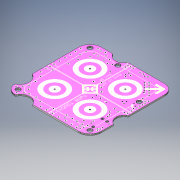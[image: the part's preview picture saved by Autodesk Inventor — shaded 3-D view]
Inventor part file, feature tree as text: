
AUTODESK INVENTOR PART (.ipt)
format: ipt  version: 2016 (Build 200138000, 138)  size: 2,645,504 bytes
history: native  units: in
note: dims shown in document units (in); Inventor stores cm internally (conversion verified against a paired STEP export)
features: other x5, sketch x2, extrude x1, move_body x1
ambient origin geometry x8: Origin, YZ Plane, XZ Plane, XY Plane, X Axis, Y Axis, Z Axis, Center Point
bodies: Solid1 (feature_tree)
feature tree (9):
  extrude  "Extrusion1"  Depth=1.453in
  move_body  "Move Body1"
  sketch  "Sketch3"  dims[d0=0.026in d1=0.0in d2=1.453in]
  other  "Decal1"
  other  "Decal2"
  other  "PCB"
  other  "Image1"
  sketch  "Sketch4"  dims[d3=90.0deg d4=90.0deg]
  other  "Image2"
